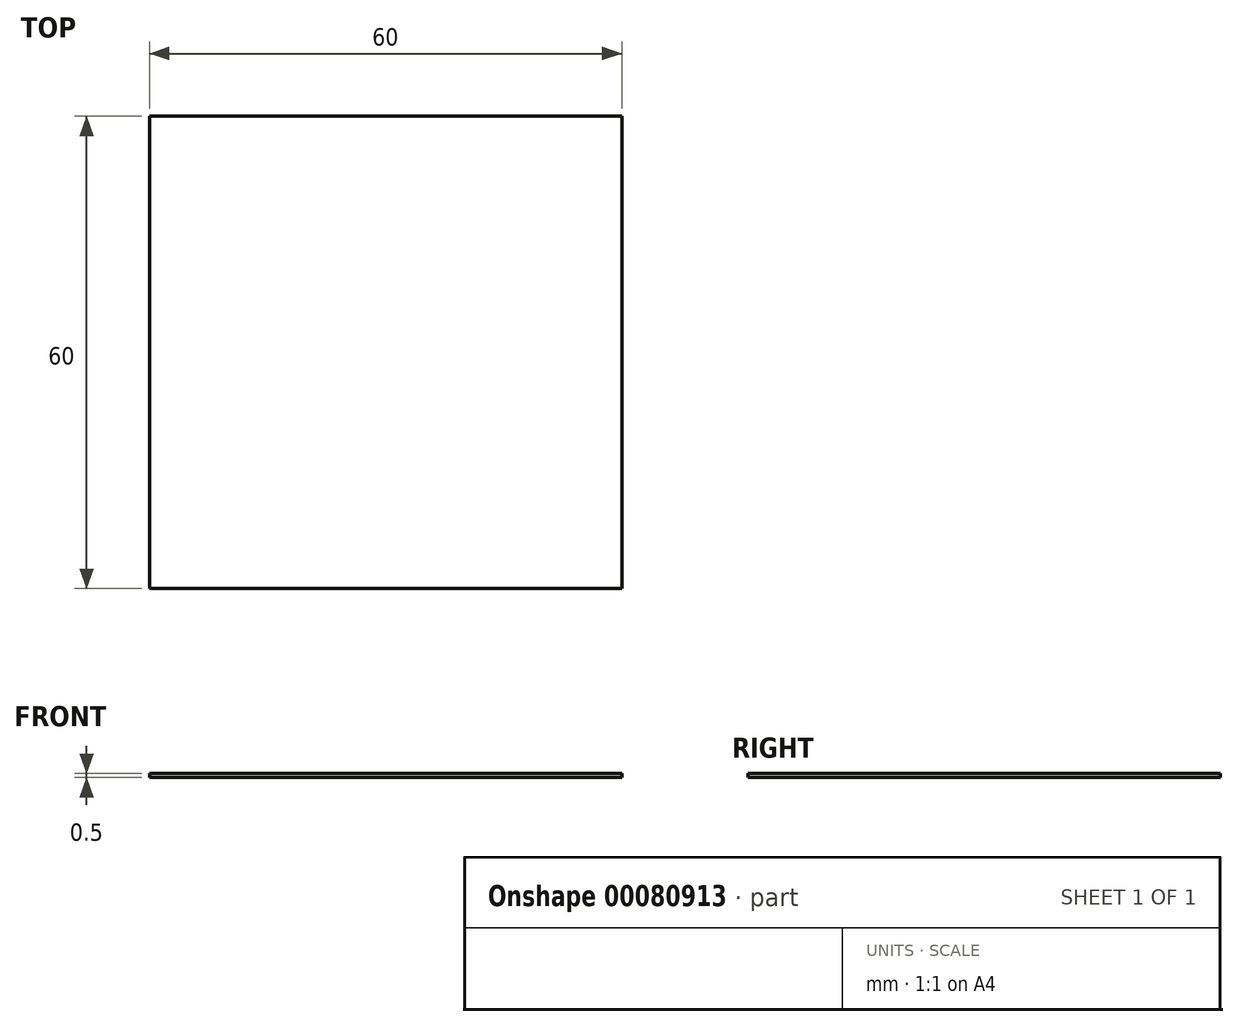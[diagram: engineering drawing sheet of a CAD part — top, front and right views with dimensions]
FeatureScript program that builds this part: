
annotation { "Feature Type Name" : "Feature", "Feature Type Description" : "" }
export const myFeature = defineFeature(function(context is Context, id is Id, definition is map)
    precondition{}
    {
        {
            var Q0;
            Q0=qCreatedBy(makeId("Top.planeOp"),FACE);
            var sketch = newSketch(context, id + "F0", { "sketchPlane" : qUnion([Q0])});
            skLineSegment(sketch, "E0.bottom", {"start": v(31.48, -30) * mm, "end": v(-28.52, -30) * mm});
            skLineSegment(sketch, "E0.top", {"start": v(31.48, 30) * mm, "end": v(-28.52, 30) * mm});
            skLineSegment(sketch, "E0.left", {"start": v(31.48, -30) * mm, "end": v(31.48, 30) * mm});
            skLineSegment(sketch, "E0.right", {"start": v(-28.52, -30) * mm, "end": v(-28.52, 30) * mm});
            skPoint(sketch, "E0.middle", {"position": v(1.48, 0) * mm});
            skSolve(sketch);
        }
        {
            var Q0;
            Q0=makeQuery(id+"F0.imprint","IMPRINT",FACE,{"disambiguationData":[TD([[makeQuery(id+"F0.imprint","IMPRINT",EDGE,{"derivedFrom":sQuery(id+"F0.wireOp",EDGE,"E0.bottom")}),-1.0]])]});
            extrude(context, id + "F1", {"entities" : qUnion([Q0]), "depth" : .5 * mm});
        }
    });
